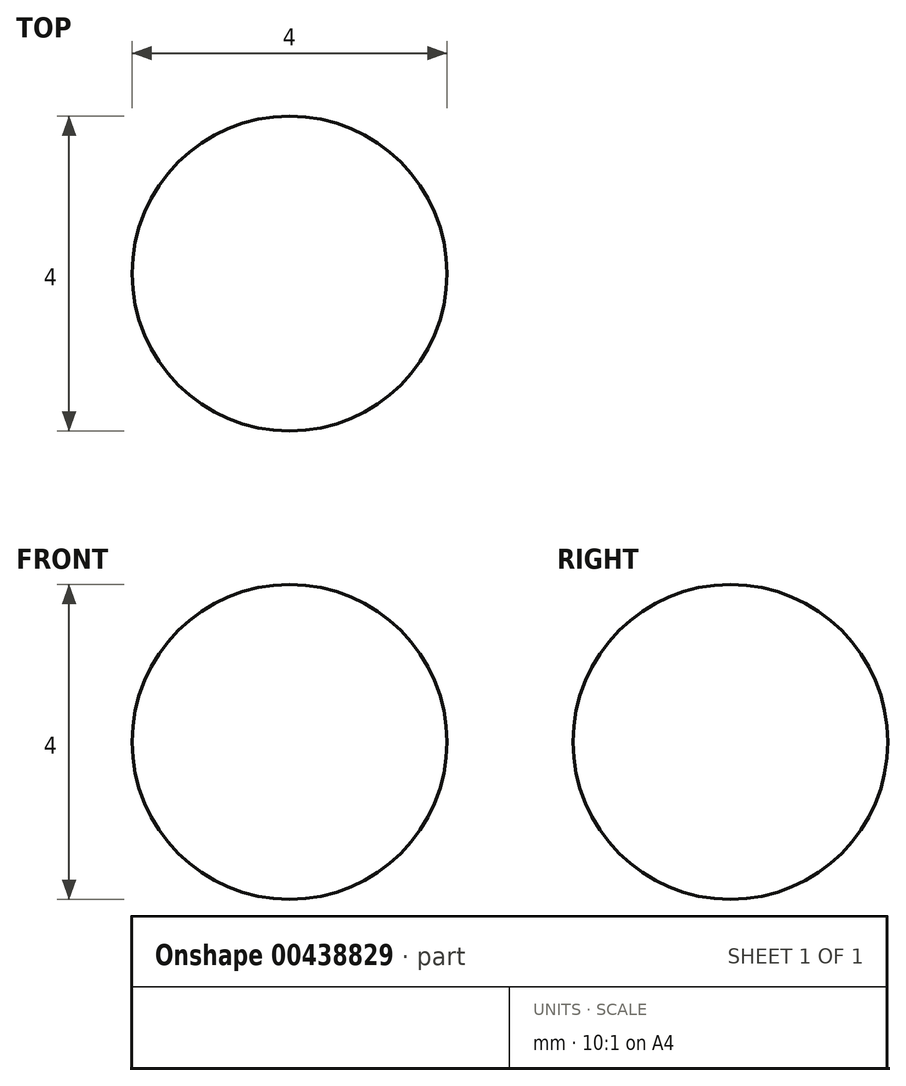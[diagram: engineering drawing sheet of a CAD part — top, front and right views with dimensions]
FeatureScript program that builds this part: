
annotation { "Feature Type Name" : "Feature", "Feature Type Description" : "" }
export const myFeature = defineFeature(function(context is Context, id is Id, definition is map)
    precondition{}
    {
        {
            var Q0;
            Q0=qCreatedBy(makeId("Top.planeOp"),FACE);
            var sketch = newSketch(context, id + "F0", { "sketchPlane" : qUnion([Q0])});
            skLineSegment(sketch, "E0", {"start": v(0, 2) * mm, "end": v(0, -2) * mm});
            skArc(sketch, "E1", {"start": v(0, -2) * mm, "mid": v(2, 0) * mm, "end": v(0, 2) * mm});
            skSolve(sketch);
        }
        {
            var Q0;
            Q0 = qSketchRegion(id + "F0", true);
            var Q1;
            Q1=sQuery(id+"F0.wireOp",EDGE,"E0");
            revolve(context, id + "F1", {"entities" : qUnion([Q0]), "axis" : qUnion([Q1]), "revolveType" : RevolveType.FULL});
        }
    });
